# Revit family: Table-Teknion-CQTCR_Routes_Rectangular_Coffee_Table-R2018
name_source: partatom
category: Furniture
revit_build: Autodesk Revit 2018 (Build: 20190510_1515(x64)
units: mm (PartAtom-declared; Revit-internal decimal feet)

## family parameters
Always vertical = Yes
Cut with Voids When Loaded = No
OmniClass Number = 23.40.20.00
OmniClass Title = General Furniture and Specialties
Room Calculation Point = No
Shared = Yes
Work Plane-Based = No

## types (2) — shared parameters
Assembly Code = E2020200
Manufacturer = Teknion
Manufacturer Fax = 416.661.4586
Part Number = CQTCR
Product Documentation Link = https://assets.teknion.com
Product Line = Routes
Product Page URL = https://www.teknion.com
Series = Routes
Sustainability Data = https://www.teknion.com
URL = www.teknion.com
Unit Weight URL = http://www.teknion.com
Warranty = http://www.teknion.com

## per-type parameters (varying)
| type | Description | Leg offset | Leg offset 2 | Model | Width |
| 24" Depth, 54" Width | Routes Rectangular Coffee Table, 24" Depth, 54" Width | 10.605 " | 13.106 " | CQTCR2454 | 54 " |
| 24" Depth, 42" Width | Routes Rectangular Coffee Table, 24" Depth, 42" Width | 6.364 " | 8.864 " | CQTCR2442 | 42 " |

## geometry (parser evidence)
native form markers: Sweep x2
no freeform markers — native parametric forms only
